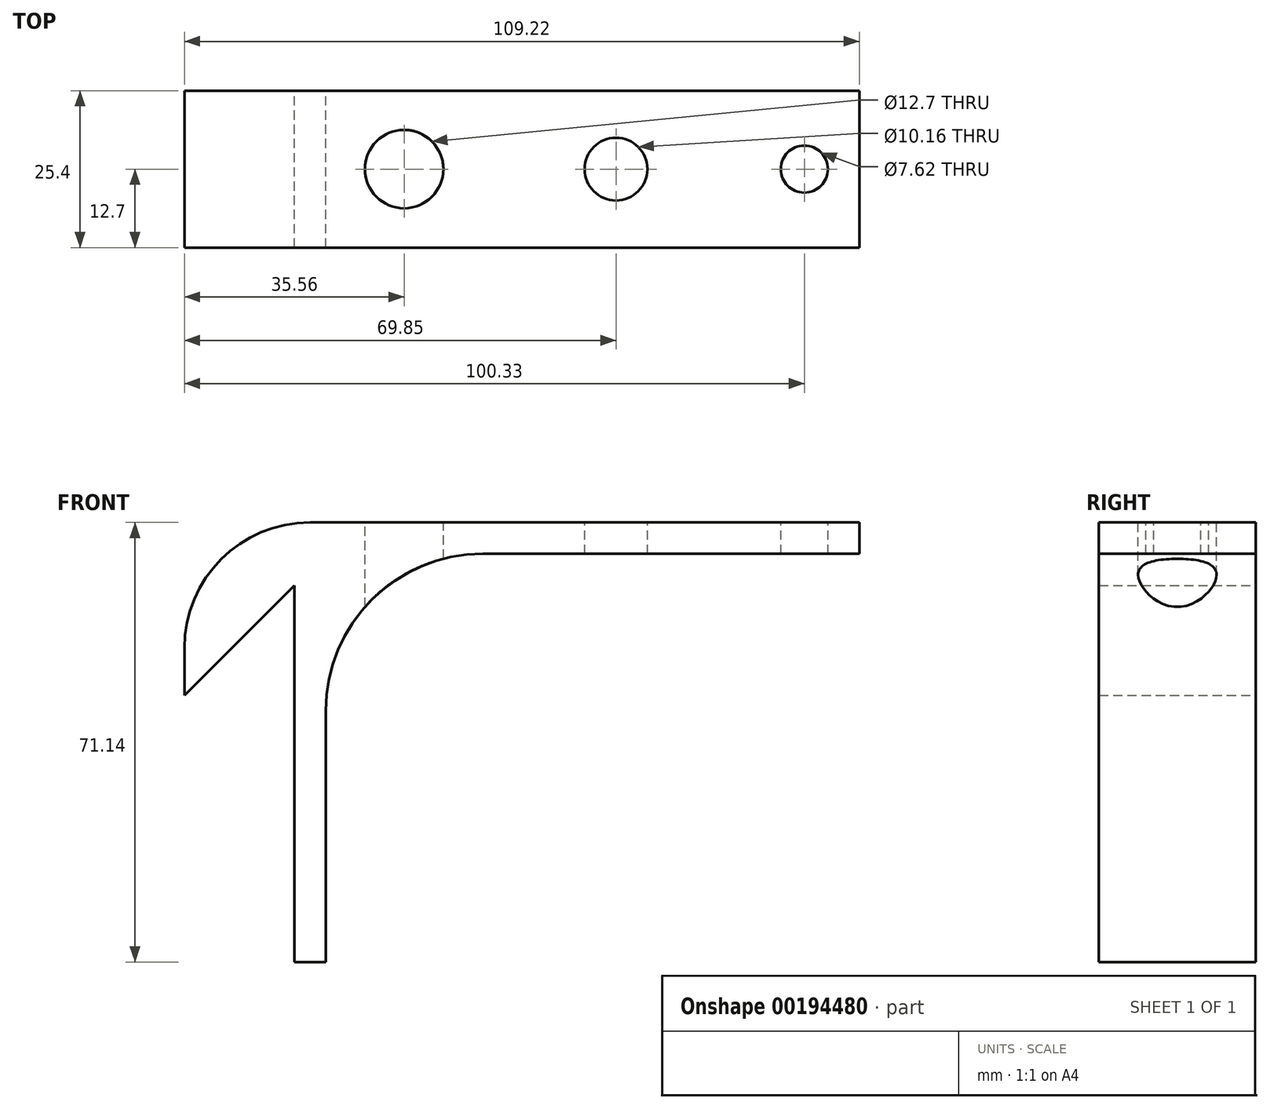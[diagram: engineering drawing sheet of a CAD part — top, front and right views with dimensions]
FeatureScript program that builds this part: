
annotation { "Feature Type Name" : "Feature", "Feature Type Description" : "" }
export const myFeature = defineFeature(function(context is Context, id is Id, definition is map)
    precondition{}
    {
        {
            var Q0;
            Q0=qCreatedBy(makeId("Front.planeOp"),FACE);
            var sketch = newSketch(context, id + "F0", { "sketchPlane" : qUnion([Q0])});
            skLineSegment(sketch, "E0", {"start": v(0, 0) * mm, "end": v(0, 38.1) * mm});
            skLineSegment(sketch, "E1", {"start": v(86.36, 66.06) * mm, "end": v(86.36, 71.14) * mm});
            skLineSegment(sketch, "E2", {"start": v(86.36, 71.14) * mm, "end": v(0, 71.14) * mm});
            skLineSegment(sketch, "E3", {"start": v(0, 71.14) * mm, "end": v(-2.54, 71.14) * mm});
            skLineSegment(sketch, "E4", {"start": v(-22.86, 50.82) * mm, "end": v(-22.86, 43.18) * mm});
            skLineSegment(sketch, "E5", {"start": v(-5.08, 0) * mm, "end": v(0, 0) * mm});
            skLineSegment(sketch, "E6", {"start": v(-5.08, 0) * mm, "end": v(-5.08, 60.96) * mm});
            skLineSegment(sketch, "E7", {"start": v(-5.08, 60.96) * mm, "end": v(-22.86, 43.18) * mm});
            skPoint(sketch, "E8.visualSharp", {"position": v(-22.86, 71.14) * mm});
            skArc(sketch, "E8.filletArc", {"start": v(-2.54, 71.14) * mm, "mid": v(-16.9, 65.19) * mm, "end": v(-22.86, 50.82) * mm});
            skLineSegment(sketch, "E9", {"start": v(86.36, 66.06) * mm, "end": v(25.4, 66.06) * mm});
            skLineSegment(sketch, "E10", {"start": v(0, 40.66) * mm, "end": v(0, 38.1) * mm});
            skPoint(sketch, "E11.visualSharp", {"position": v(0, 66.06) * mm});
            skArc(sketch, "E11.filletArc", {"start": v(25.4, 66.06) * mm, "mid": v(7.44, 58.62) * mm, "end": v(0, 40.66) * mm});
            skSolve(sketch);
        }
        {
            var Q0;
            Q0=makeQuery(id+"F0.imprint","IMPRINT",FACE,{"disambiguationData":[TD([[makeQuery(id+"F0.imprint","IMPRINT",EDGE,{"derivedFrom":sQuery(id+"F0.wireOp",EDGE,"E0")}),1.0]])]});
            var Q1;
            Q1 = qSketchRegion(id + "F2", true);
            extrude(context, id + "F1", {"entities" : qUnion([Q0, Q1]), "depth" : 25.4 * mm});
        }
        {
            var Q0;
            Q0=makeQuery(id+"F1.opExtrude","SWEPT_FACE",FACE,{"disambiguationData":[OSD([sQuery(id+"F0.wireOp",EDGE,"E2"),sQuery(id+"F0.wireOp",EDGE,"E3")])]});
            var sketch = newSketch(context, id + "F2", { "sketchPlane" : qUnion([Q0])});
            skCircle(sketch, "E12", {"center": v(77.47, -12.7) * mm, "radius": 3.81 * mm});
            skPoint(sketch, "E12.centerSnap0", {"position": v(86.36, -12.7) * mm});
            skCircle(sketch, "E13.1.0.0", {"center": v(47, -12.7) * mm, "radius": 5.08 * mm});
            skCircle(sketch, "E13.2.0.0", {"center": v(12.7, -12.7) * mm, "radius": 6.35 * mm});
            skLineSegment(sketch, "E13.direction1", {"start": v(77.47, -12.7) * mm, "end": v(47, -12.7) * mm, "construction": true});
            skSolve(sketch);
        }
        {
            var Q0;
            Q0=makeQuery(id+"F2.imprint","IMPRINT",FACE,{"disambiguationData":[TD([[makeQuery(id+"F2.imprint","IMPRINT",EDGE,{"derivedFrom":sQuery(id+"F2.wireOp",EDGE,"E12")}),1.0]])]});
            var Q1;
            Q1=makeQuery(id+"F2.imprint","IMPRINT",FACE,{"disambiguationData":[TD([[makeQuery(id+"F2.imprint","IMPRINT",EDGE,{"derivedFrom":sQuery(id+"F2.wireOp",EDGE,"E13.1.0.0")}),1.0]])]});
            var Q2;
            Q2=makeQuery(id+"F2.imprint","IMPRINT",FACE,{"disambiguationData":[TD([[makeQuery(id+"F2.imprint","IMPRINT",EDGE,{"derivedFrom":sQuery(id+"F2.wireOp",EDGE,"E13.2.0.0")}),1.0]])]});
            extrude(context, id + "F3", {"entities" : qUnion([Q0, Q1, Q2]), "operationType" : NewBodyOperationType.REMOVE, "endBound" : BoundingType.THROUGH_ALL, "oppositeDirection" : true, "depth" : 25.4 * mm});
        }
    });
